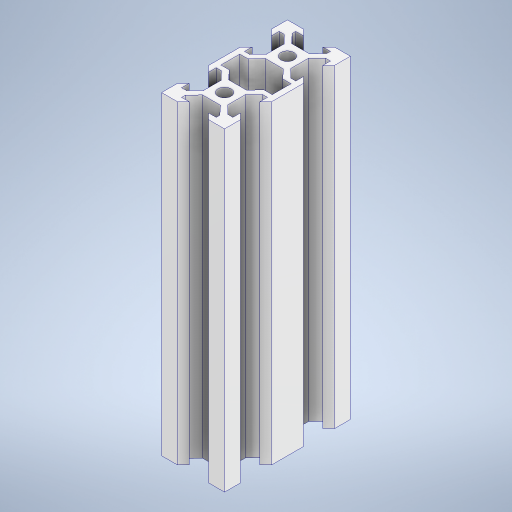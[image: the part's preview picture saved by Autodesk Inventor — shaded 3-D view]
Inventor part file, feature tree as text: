
AUTODESK INVENTOR PART (.ipt)
format: ipt  version: 2023 (Build 270158000, 158)  size: 324,096 bytes
history: native  units: mm
features: extrude x1, sketch x1
ambient origin geometry x8: Origin, YZ Plane, XZ Plane, XY Plane, X Axis, Y Axis, Z Axis, Center Point
bodies: Solid2 (feature_tree), Solid1 (feature_tree)
feature tree (2):
  extrude  "Extrusion1"  [1 undecoded]
  sketch  "Sketch1"  dims[d0=175.0mm d1=0.0mm]
note: 1 required parameter value undecoded (feature->parameter linkage not recoverable at this tier; creation-order binding heuristic only, values carry confidence <= 0.55)
